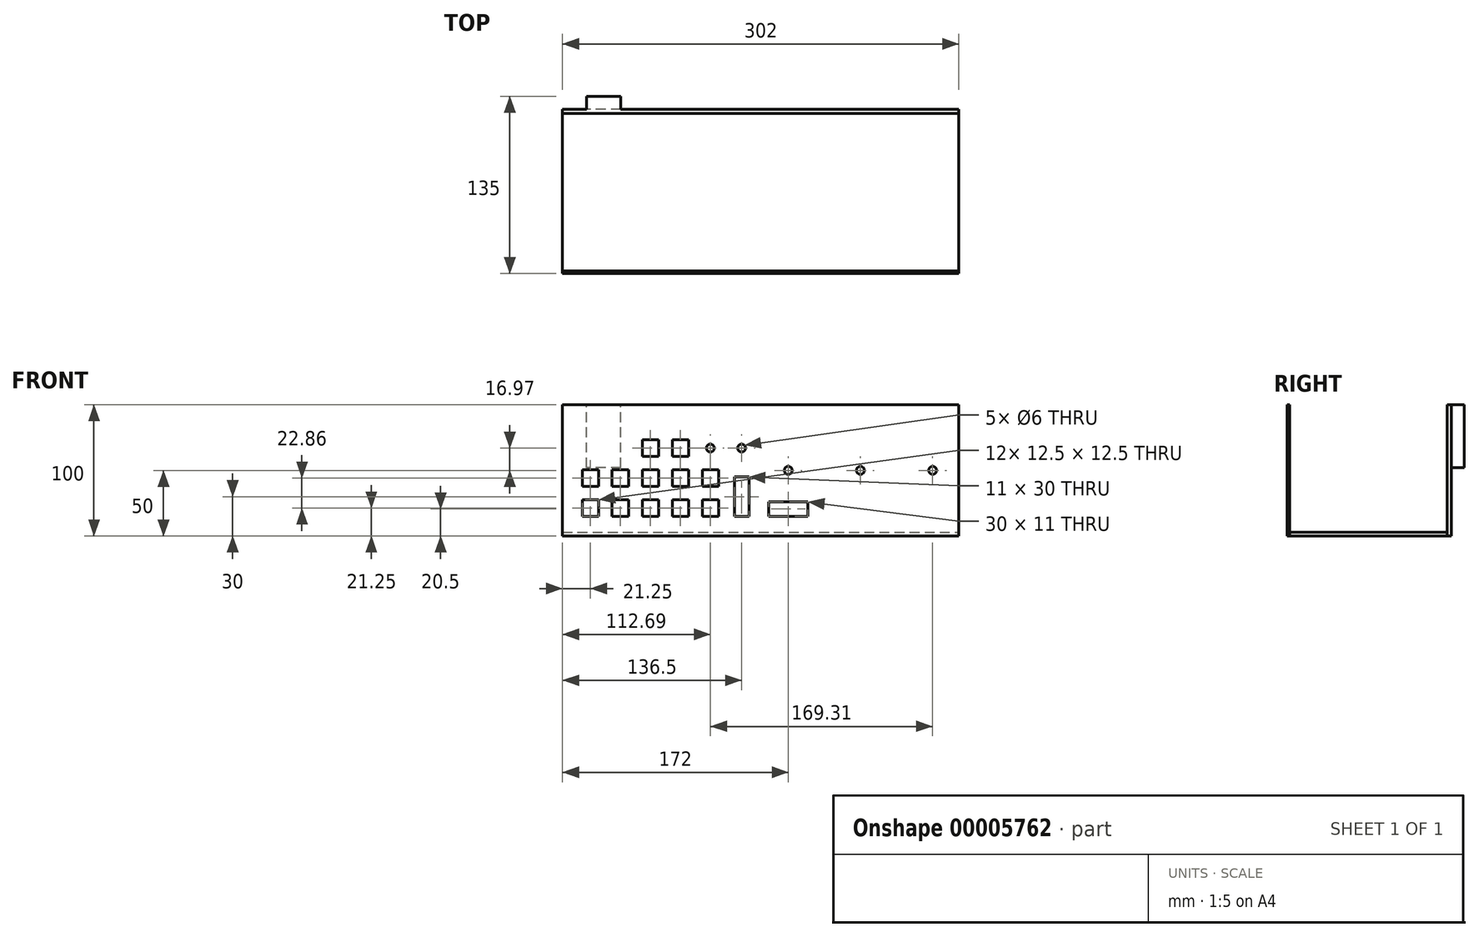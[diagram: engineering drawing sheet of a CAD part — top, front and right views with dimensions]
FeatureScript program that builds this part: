
annotation { "Feature Type Name" : "Feature", "Feature Type Description" : "" }
export const myFeature = defineFeature(function(context is Context, id is Id, definition is map)
    precondition{}
    {
        {
            var Q0;
            Q0=qCreatedBy(makeId("Front.planeOp"),FACE);
            var sketch = newSketch(context, id + "F0", { "sketchPlane" : qUnion([Q0])});
            skLineSegment(sketch, "E0.bottom", {"start": v(0, 0) * mm, "end": v(302, 0) * mm});
            skLineSegment(sketch, "E0.top", {"start": v(0, 100) * mm, "end": v(302, 100) * mm});
            skLineSegment(sketch, "E0.left", {"start": v(0, 0) * mm, "end": v(0, 100) * mm});
            skLineSegment(sketch, "E0.right", {"start": v(302, 0) * mm, "end": v(302, 100) * mm});
            skSolve(sketch);
        }
        {
            var Q0;
            Q0 = qSketchRegion(id + "F0", true);
            extrude(context, id + "F1", {"entities" : qUnion([Q0]), "depth" : 2 * mm});
        }
        {
            var Q0;
            Q0=makeQuery(id+"F1.opExtrude","CAP_FACE",FACE,{"disambiguationData":[OSD([sQuery(id+"F0.wireOp",EDGE,"E0.bottom"),sQuery(id+"F0.wireOp",EDGE,"E0.top"),sQuery(id+"F0.wireOp",EDGE,"E0.left"),sQuery(id+"F0.wireOp",EDGE,"E0.right")])],"isStart":false});
            var sketch = newSketch(context, id + "F2", { "sketchPlane" : qUnion([Q0])});
            skLineSegment(sketch, "E1.bottom", {"start": v(15, 27.5) * mm, "end": v(27.5, 27.5) * mm});
            skLineSegment(sketch, "E1.top", {"start": v(15, 15) * mm, "end": v(27.5, 15) * mm});
            skLineSegment(sketch, "E1.left", {"start": v(15, 27.5) * mm, "end": v(15, 15) * mm});
            skLineSegment(sketch, "E1.right", {"start": v(27.5, 27.5) * mm, "end": v(27.5, 15) * mm});
            skLineSegment(sketch, "E2.0.1.0", {"start": v(27.5, 50.36) * mm, "end": v(27.5, 37.86) * mm});
            skLineSegment(sketch, "E2.0.1.1", {"start": v(15, 50.36) * mm, "end": v(27.5, 50.36) * mm});
            skLineSegment(sketch, "E2.0.1.2", {"start": v(15, 50.36) * mm, "end": v(15, 37.86) * mm});
            skLineSegment(sketch, "E2.0.1.3", {"start": v(15, 37.86) * mm, "end": v(27.5, 37.86) * mm});
            skLineSegment(sketch, "E2.1.0.0", {"start": v(50.36, 27.5) * mm, "end": v(50.36, 15) * mm});
            skLineSegment(sketch, "E2.1.0.1", {"start": v(37.86, 27.5) * mm, "end": v(50.36, 27.5) * mm});
            skLineSegment(sketch, "E2.1.0.2", {"start": v(37.86, 27.5) * mm, "end": v(37.86, 15) * mm});
            skLineSegment(sketch, "E2.1.0.3", {"start": v(37.86, 15) * mm, "end": v(50.36, 15) * mm});
            skLineSegment(sketch, "E2.1.1.0", {"start": v(50.36, 50.36) * mm, "end": v(50.36, 37.86) * mm});
            skLineSegment(sketch, "E2.1.1.1", {"start": v(37.86, 50.36) * mm, "end": v(50.36, 50.36) * mm});
            skLineSegment(sketch, "E2.1.1.2", {"start": v(37.86, 50.36) * mm, "end": v(37.86, 37.86) * mm});
            skLineSegment(sketch, "E2.1.1.3", {"start": v(37.86, 37.86) * mm, "end": v(50.36, 37.86) * mm});
            skLineSegment(sketch, "E2.2.0.0", {"start": v(73.22, 27.5) * mm, "end": v(73.22, 15) * mm});
            skLineSegment(sketch, "E2.2.0.1", {"start": v(60.72, 27.5) * mm, "end": v(73.22, 27.5) * mm});
            skLineSegment(sketch, "E2.2.0.2", {"start": v(60.72, 27.5) * mm, "end": v(60.72, 15) * mm});
            skLineSegment(sketch, "E2.2.0.3", {"start": v(60.72, 15) * mm, "end": v(73.22, 15) * mm});
            skLineSegment(sketch, "E2.2.1.0", {"start": v(73.22, 50.36) * mm, "end": v(73.22, 37.86) * mm});
            skLineSegment(sketch, "E2.2.1.1", {"start": v(60.72, 50.36) * mm, "end": v(73.22, 50.36) * mm});
            skLineSegment(sketch, "E2.2.1.2", {"start": v(60.72, 50.36) * mm, "end": v(60.72, 37.86) * mm});
            skLineSegment(sketch, "E2.2.1.3", {"start": v(60.72, 37.86) * mm, "end": v(73.22, 37.86) * mm});
            skLineSegment(sketch, "E2.3.0.0", {"start": v(96.08, 27.5) * mm, "end": v(96.08, 15) * mm});
            skLineSegment(sketch, "E2.3.0.1", {"start": v(83.58, 27.5) * mm, "end": v(96.08, 27.5) * mm});
            skLineSegment(sketch, "E2.3.0.2", {"start": v(83.58, 27.5) * mm, "end": v(83.58, 15) * mm});
            skLineSegment(sketch, "E2.3.0.3", {"start": v(83.58, 15) * mm, "end": v(96.08, 15) * mm});
            skLineSegment(sketch, "E2.3.1.0", {"start": v(96.08, 50.36) * mm, "end": v(96.08, 37.86) * mm});
            skLineSegment(sketch, "E2.3.1.1", {"start": v(83.58, 50.36) * mm, "end": v(96.08, 50.36) * mm});
            skLineSegment(sketch, "E2.3.1.2", {"start": v(83.58, 50.36) * mm, "end": v(83.58, 37.86) * mm});
            skLineSegment(sketch, "E2.3.1.3", {"start": v(83.58, 37.86) * mm, "end": v(96.08, 37.86) * mm});
            skLineSegment(sketch, "E2.4.0.0", {"start": v(118.94, 27.5) * mm, "end": v(118.94, 15) * mm});
            skLineSegment(sketch, "E2.4.0.1", {"start": v(106.44, 27.5) * mm, "end": v(118.94, 27.5) * mm});
            skLineSegment(sketch, "E2.4.0.2", {"start": v(106.44, 27.5) * mm, "end": v(106.44, 15) * mm});
            skLineSegment(sketch, "E2.4.0.3", {"start": v(106.44, 15) * mm, "end": v(118.94, 15) * mm});
            skLineSegment(sketch, "E2.4.1.0", {"start": v(118.94, 50.36) * mm, "end": v(118.94, 37.86) * mm});
            skLineSegment(sketch, "E2.4.1.1", {"start": v(106.44, 50.36) * mm, "end": v(118.94, 50.36) * mm});
            skLineSegment(sketch, "E2.4.1.2", {"start": v(106.44, 50.36) * mm, "end": v(106.44, 37.86) * mm});
            skLineSegment(sketch, "E2.4.1.3", {"start": v(106.44, 37.86) * mm, "end": v(118.94, 37.86) * mm});
            skLineSegment(sketch, "E2.direction1", {"start": v(27.5, 15) * mm, "end": v(50.36, 15) * mm, "construction": true});
            skLineSegment(sketch, "E2.direction2", {"start": v(27.5, 15) * mm, "end": v(27.5, 37.86) * mm, "construction": true});
            skLineSegment(sketch, "E3.0.1.0", {"start": v(83.58, 73.22) * mm, "end": v(96.08, 73.22) * mm});
            skLineSegment(sketch, "E3.0.1.1", {"start": v(96.08, 73.22) * mm, "end": v(96.08, 60.72) * mm});
            skLineSegment(sketch, "E3.0.1.2", {"start": v(83.58, 60.72) * mm, "end": v(96.08, 60.72) * mm});
            skLineSegment(sketch, "E3.0.1.3", {"start": v(83.58, 73.22) * mm, "end": v(83.58, 60.72) * mm});
            skLineSegment(sketch, "E3.0.1.4", {"start": v(73.22, 73.22) * mm, "end": v(73.22, 60.72) * mm});
            skLineSegment(sketch, "E3.0.1.5", {"start": v(60.72, 60.72) * mm, "end": v(73.22, 60.72) * mm});
            skLineSegment(sketch, "E3.0.1.6", {"start": v(60.72, 73.22) * mm, "end": v(60.72, 60.72) * mm});
            skLineSegment(sketch, "E3.0.1.7", {"start": v(60.72, 73.22) * mm, "end": v(73.22, 73.22) * mm});
            skLineSegment(sketch, "E3.direction1", {"start": v(83.58, 50.36) * mm, "end": v(99.58, 50.36) * mm, "construction": true});
            skLineSegment(sketch, "E3.direction2", {"start": v(83.58, 50.36) * mm, "end": v(83.58, 73.22) * mm, "construction": true});
            skSolve(sketch);
        }
        {
            var Q0;
            Q0 = qSketchRegion(id + "F2", true);
            extrude(context, id + "F3", {"entities" : qUnion([Q0]), "operationType" : NewBodyOperationType.REMOVE, "endBound" : BoundingType.THROUGH_ALL, "oppositeDirection" : true, "depth" : 25 * mm});
        }
        {
            var Q0;
            Q0=makeQuery(id+"F1.opExtrude","CAP_FACE",FACE,{"disambiguationData":[OSD([sQuery(id+"F0.wireOp",EDGE,"E0.bottom"),sQuery(id+"F0.wireOp",EDGE,"E0.top"),sQuery(id+"F0.wireOp",EDGE,"E0.left"),sQuery(id+"F0.wireOp",EDGE,"E0.right")])],"isStart":false});
            var sketch = newSketch(context, id + "F4", { "sketchPlane" : qUnion([Q0])});
            skLineSegment(sketch, "E4.bottom", {"start": v(157, 26) * mm, "end": v(187, 26) * mm});
            skLineSegment(sketch, "E4.top", {"start": v(157, 15) * mm, "end": v(187, 15) * mm});
            skLineSegment(sketch, "E4.left", {"start": v(157, 26) * mm, "end": v(157, 15) * mm});
            skLineSegment(sketch, "E4.right", {"start": v(187, 26) * mm, "end": v(187, 15) * mm});
            skLineSegment(sketch, "E5.bottom", {"start": v(131, 45) * mm, "end": v(142, 45) * mm});
            skLineSegment(sketch, "E5.top", {"start": v(131, 15) * mm, "end": v(142, 15) * mm});
            skLineSegment(sketch, "E5.left", {"start": v(131, 45) * mm, "end": v(131, 15) * mm});
            skLineSegment(sketch, "E5.right", {"start": v(142, 45) * mm, "end": v(142, 15) * mm});
            skSolve(sketch);
        }
        {
            var Q0;
            Q0 = qSketchRegion(id + "F4", true);
            extrude(context, id + "F5", {"entities" : qUnion([Q0]), "operationType" : NewBodyOperationType.REMOVE, "endBound" : BoundingType.THROUGH_ALL, "oppositeDirection" : true, "depth" : 25 * mm});
        }
        {
            var Q0;
            Q0=makeQuery(id+"F1.opExtrude","CAP_FACE",FACE,{"disambiguationData":[OSD([sQuery(id+"F0.wireOp",EDGE,"E0.bottom"),sQuery(id+"F0.wireOp",EDGE,"E0.top"),sQuery(id+"F0.wireOp",EDGE,"E0.left"),sQuery(id+"F0.wireOp",EDGE,"E0.right")])],"isStart":false});
            var sketch = newSketch(context, id + "F6", { "sketchPlane" : qUnion([Q0])});
            skCircle(sketch, "E6", {"center": v(282, 50) * mm, "radius": 3 * mm});
            skCircle(sketch, "E7", {"center": v(227, 50) * mm, "radius": 3 * mm});
            skCircle(sketch, "E8", {"center": v(172, 50) * mm, "radius": 3 * mm});
            skSolve(sketch);
        }
        {
            var Q0;
            Q0 = qSketchRegion(id + "F6", true);
            extrude(context, id + "F7", {"entities" : qUnion([Q0]), "operationType" : NewBodyOperationType.REMOVE, "endBound" : BoundingType.THROUGH_ALL, "oppositeDirection" : true, "depth" : 25 * mm});
        }
        {
            var Q0;
            Q0=makeQuery(id+"F1.opExtrude","CAP_FACE",FACE,{"disambiguationData":[OSD([sQuery(id+"F0.wireOp",EDGE,"E0.bottom"),sQuery(id+"F0.wireOp",EDGE,"E0.top"),sQuery(id+"F0.wireOp",EDGE,"E0.left"),sQuery(id+"F0.wireOp",EDGE,"E0.right")])],"isStart":false});
            var sketch = newSketch(context, id + "F8", { "sketchPlane" : qUnion([Q0])});
            skCircle(sketch, "E9", {"center": v(136.5, 66.97) * mm, "radius": 3 * mm});
            skLineSegment(sketch, "E10", {"start": v(136.5, 15) * mm, "end": v(136.5, 100) * mm, "construction": true});
            skCircle(sketch, "E11", {"center": v(112.7, 66.97) * mm, "radius": 3 * mm});
            skLineSegment(sketch, "E12", {"start": v(112.7, 50.36) * mm, "end": v(112.7, 100) * mm, "construction": true});
            skLineSegment(sketch, "E13", {"start": v(96.08, 66.97) * mm, "end": v(302, 66.97) * mm, "construction": true});
            skSolve(sketch);
        }
        {
            var Q0;
            Q0 = qSketchRegion(id + "F8", true);
            extrude(context, id + "F9", {"entities" : qUnion([Q0]), "operationType" : NewBodyOperationType.REMOVE, "endBound" : BoundingType.THROUGH_ALL, "oppositeDirection" : true, "depth" : 25 * mm});
        }
        {
            var Q0;
            Q0=makeQuery(id+"F1.opExtrude","CAP_FACE",FACE,{"disambiguationData":[OSD([sQuery(id+"F0.wireOp",EDGE,"E0.bottom"),sQuery(id+"F0.wireOp",EDGE,"E0.top"),sQuery(id+"F0.wireOp",EDGE,"E0.left"),sQuery(id+"F0.wireOp",EDGE,"E0.right")])],"isStart":true});
            var sketch = newSketch(context, id + "F10", { "sketchPlane" : qUnion([Q0])});
            skLineSegment(sketch, "E14.bottom", {"start": v(0, 0) * mm, "end": v(-302, 0) * mm});
            skLineSegment(sketch, "E14.top", {"start": v(0, 3) * mm, "end": v(-302, 3) * mm});
            skLineSegment(sketch, "E14.left", {"start": v(0, 0) * mm, "end": v(0, 3) * mm});
            skLineSegment(sketch, "E14.right", {"start": v(-302, 0) * mm, "end": v(-302, 3) * mm});
            skSolve(sketch);
        }
        {
            var Q0;
            Q0 = qSketchRegion(id + "F10", true);
            extrude(context, id + "F11", {"entities" : qUnion([Q0]), "depth" : 120 * mm});
        }
        {
            var Q0;
            Q0=makeQuery(id+"F11.opExtrude","CAP_FACE",FACE,{"disambiguationData":[OSD([sQuery(id+"F10.wireOp",EDGE,"E14.bottom"),sQuery(id+"F10.wireOp",EDGE,"E14.top"),sQuery(id+"F10.wireOp",EDGE,"E14.left"),sQuery(id+"F10.wireOp",EDGE,"E14.right")])],"isStart":false});
            var sketch = newSketch(context, id + "F12", { "sketchPlane" : qUnion([Q0])});
            skLineSegment(sketch, "E15.bottom", {"start": v(0, 0) * mm, "end": v(-302, 0) * mm});
            skLineSegment(sketch, "E15.left", {"start": v(0, 0) * mm, "end": v(0, 100) * mm});
            skLineSegment(sketch, "E15.right", {"start": v(-302, 0) * mm, "end": v(-302, 100) * mm});
            skLineSegment(sketch, "E16.0", {"start": v(0, 100) * mm, "end": v(-302, 100) * mm});
            skSolve(sketch);
        }
        {
            var Q0;
            Q0 = qSketchRegion(id + "F12", true);
            extrude(context, id + "F13", {"entities" : qUnion([Q0]), "depth" : 3 * mm});
        }
        {
            var Q0;
            Q0=makeQuery(id+"F13.opExtrude","CAP_FACE",FACE,{"disambiguationData":[OSD([sQuery(id+"F12.wireOp",EDGE,"E15.bottom"),sQuery(id+"F12.wireOp",EDGE,"E15.left"),sQuery(id+"F12.wireOp",EDGE,"E15.right"),sQuery(id+"F12.wireOp",EDGE,"E16.0")])],"isStart":false});
            var sketch = newSketch(context, id + "F14", { "sketchPlane" : qUnion([Q0])});
            skLineSegment(sketch, "E17.bottom", {"start": v(-44.42, 52.23) * mm, "end": v(-18.24, 52.23) * mm});
            skLineSegment(sketch, "E17.top", {"start": v(-44.42, 100) * mm, "end": v(-18.24, 100) * mm});
            skLineSegment(sketch, "E17.left", {"start": v(-44.42, 52.23) * mm, "end": v(-44.42, 100) * mm});
            skLineSegment(sketch, "E17.right", {"start": v(-18.24, 52.23) * mm, "end": v(-18.24, 100) * mm});
            skSolve(sketch);
        }
        {
            var Q0;
            Q0=makeQuery(id+"F14.imprint","IMPRINT",FACE,{"disambiguationData":[TD([[makeQuery(id+"F14.imprint","IMPRINT",EDGE,{"derivedFrom":sQuery(id+"F14.wireOp",EDGE,"E17.bottom")}),1.0]])]});
            extrude(context, id + "F15", {"entities" : qUnion([Q0]), "operationType" : NewBodyOperationType.ADD, "depth" : 10 * mm, "offsetDistance" : 25 * mm});
        }
    });
